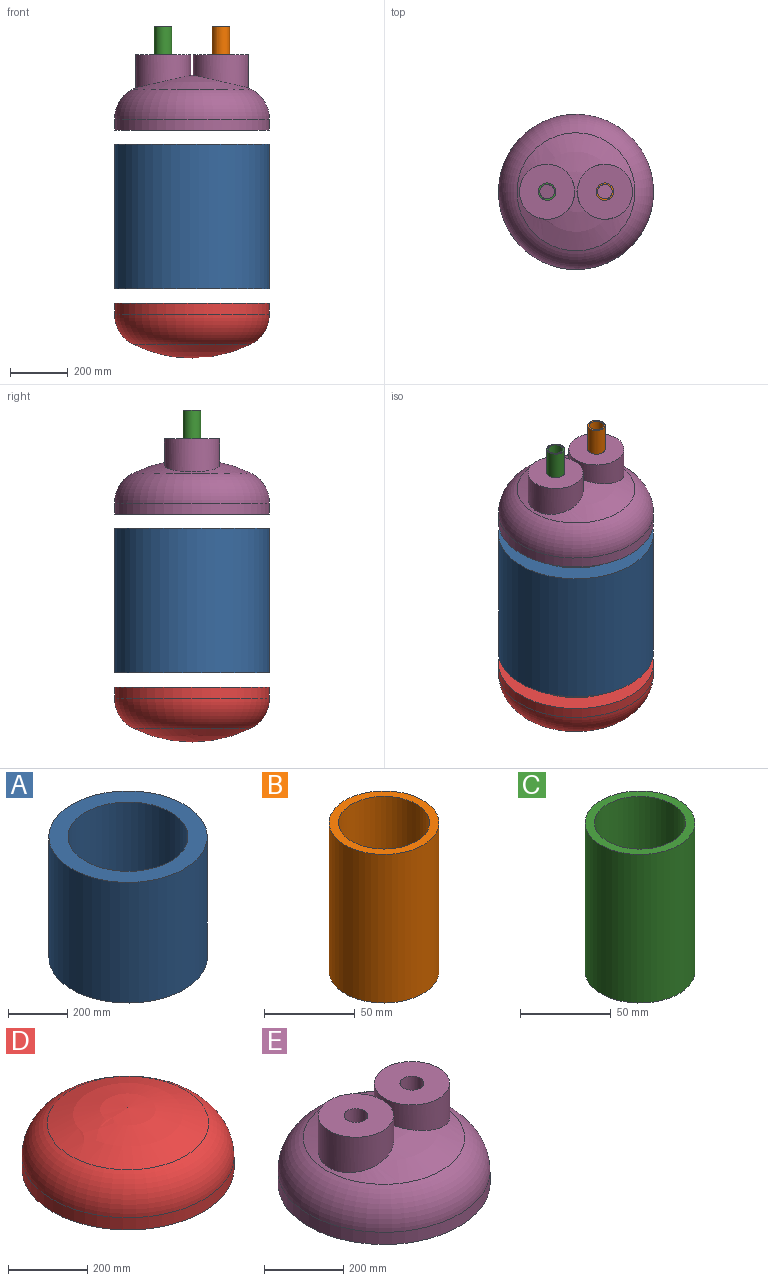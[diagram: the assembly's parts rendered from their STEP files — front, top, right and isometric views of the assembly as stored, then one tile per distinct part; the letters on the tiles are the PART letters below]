
ASSEMBLY  parts=5 mates=4
PART A: 4 faces, bbox 536.4x536.4x500 mm
  f0: cylinder r=203.2mm len=500mm, axis (0,0,-1), area 638371.6mm2, adj f2,f3
  f1: cylinder r=268.2mm len=536.4mm, axis (0,0,-1), area 842575.1mm2, adj f2,f3
  f2: plane 536.4x536.4mm, normal (0,0,1), area 96261.5mm2, adj f0,f1
  f3: plane 536.4x536.4mm, normal (0,0,-1), area 96261.5mm2, adj f0,f1
PART B: 4 faces, bbox 60.5x60.5x100 mm
  f0: cylinder r=25.05mm len=100mm, axis (0,0,-1), area 15739.4mm2, adj f2,f3
  f1: cylinder r=30.25mm len=100mm, axis (0,0,-1), area 19006.6mm2, adj f2,f3
  f2: plane 60.5x60.5mm, normal (0,0,1), area 903.4mm2, adj f0,f1
  f3: plane 60.5x60.5mm, normal (0,0,-1), area 903.4mm2, adj f0,f1
PART C: 4 faces, bbox 60.5x60.5x100 mm
  f0: cylinder r=25.05mm len=100mm, axis (0,0,-1), area 15739.4mm2, adj f2,f3
  f1: cylinder r=30.25mm len=100mm, axis (0,0,-1), area 19006.6mm2, adj f2,f3
  f2: plane 60.5x60.5mm, normal (0,0,1), area 903.4mm2, adj f0,f1
  f3: plane 60.5x60.5mm, normal (0,0,-1), area 903.4mm2, adj f0,f1
PART D: 7 faces, bbox 580.6x580.6x232.9 mm
  f0: plane 536.4x536.4mm, normal (0,0,-1), area 96261.5mm2, adj f1,f6
  f1: cylinder r=268.2mm len=536.4mm, axis (0,0,-1), area 63868.4mm2, adj f0,f2
  f2: torus R=152.96mm, axis (0,0,-1), area 197712.4mm2, adj f1,f3
  f3: sphere r=459.4mm, area 138166.5mm2, adj f2
  f4: sphere r=394.4mm, area 101834.4mm2, adj f5
  f5: torus R=152.96mm, axis (0,0,-1), area 67814.2mm2, adj f4,f6
  f6: cylinder r=203.2mm len=406.4mm, axis (0,0,-1), area 48389.5mm2, adj f0,f5
PART E: 15 faces, bbox 580.6x580.6x303.9 mm
  f0: sphere r=459.4mm, area 79039.3mm2, adj f3,f8,f12
  f1: plane 536.4x536.4mm, normal (0,0,-1), area 96261.5mm2, adj f2,f6
  f2: cylinder r=268.2mm len=536.4mm, axis (0,0,-1), area 63868.4mm2, adj f1,f3
  f3: torus R=152.96mm, axis (0,0,-1), area 197712.4mm2, adj f0,f2
  f4: sphere r=394.4mm, area 101834.4mm2, adj f5
  f5: torus R=152.96mm, axis (0,0,-1), area 67814.2mm2, adj f4,f6
  f6: cylinder r=203.2mm len=406.4mm, axis (0,0,-1), area 48389.5mm2, adj f1,f5
  f7: plane 190.5x190.5mm, normal (0,0,1), area 25627.5mm2, adj f8,f9
  f8: cylinder r=95.25mm len=190.5mm, axis (0,0,1), area 55371.3mm2, adj f0,f7
  f9: cylinder r=30.25mm len=89.85mm, axis (0,0,1), area 15787.6mm2, adj f7,f10
  f10: sphere r=459.4mm, area 2948.9mm2, adj f9
  f11: plane 190.5x190.5mm, normal (0,0,1), area 25627.5mm2, adj f12,f13
  f12: cylinder r=95.25mm len=190.5mm, axis (0,0,1), area 55371.7mm2, adj f0,f11
  f13: cylinder r=30.25mm len=89.85mm, axis (0,0,1), area 15787.3mm2, adj f11,f14
  f14: sphere r=459.4mm, area 2949.3mm2, adj f13
PLACE A t=(-199.33,-137.11,-33.04)mm
PLACE B t=(-199.33,-137.11,266.96)mm
PLACE C t=(-199.33,-137.11,266.96)mm
PLACE D rot(axis=(1,0,0),180deg) t=(-199.33,-137.11,-333.04)mm
PLACE E t=(-199.33,-137.11,266.96)mm
MATE revolute C.f1 <-> E.f13  axis (0,0,-1) through (-299.33,-137.11,526.96)mm
MATE revolute E.f2 <-> A.f1  axis (0,0,-1) through (-199.33,-137.11,266.96)mm
MATE revolute B.f1 <-> E.f9  axis (0,0,-1) through (-99.33,-137.11,526.96)mm
MATE revolute D.f1 <-> A.f0  axis (0,0,1) through (-199.33,-137.11,-333.04)mm
